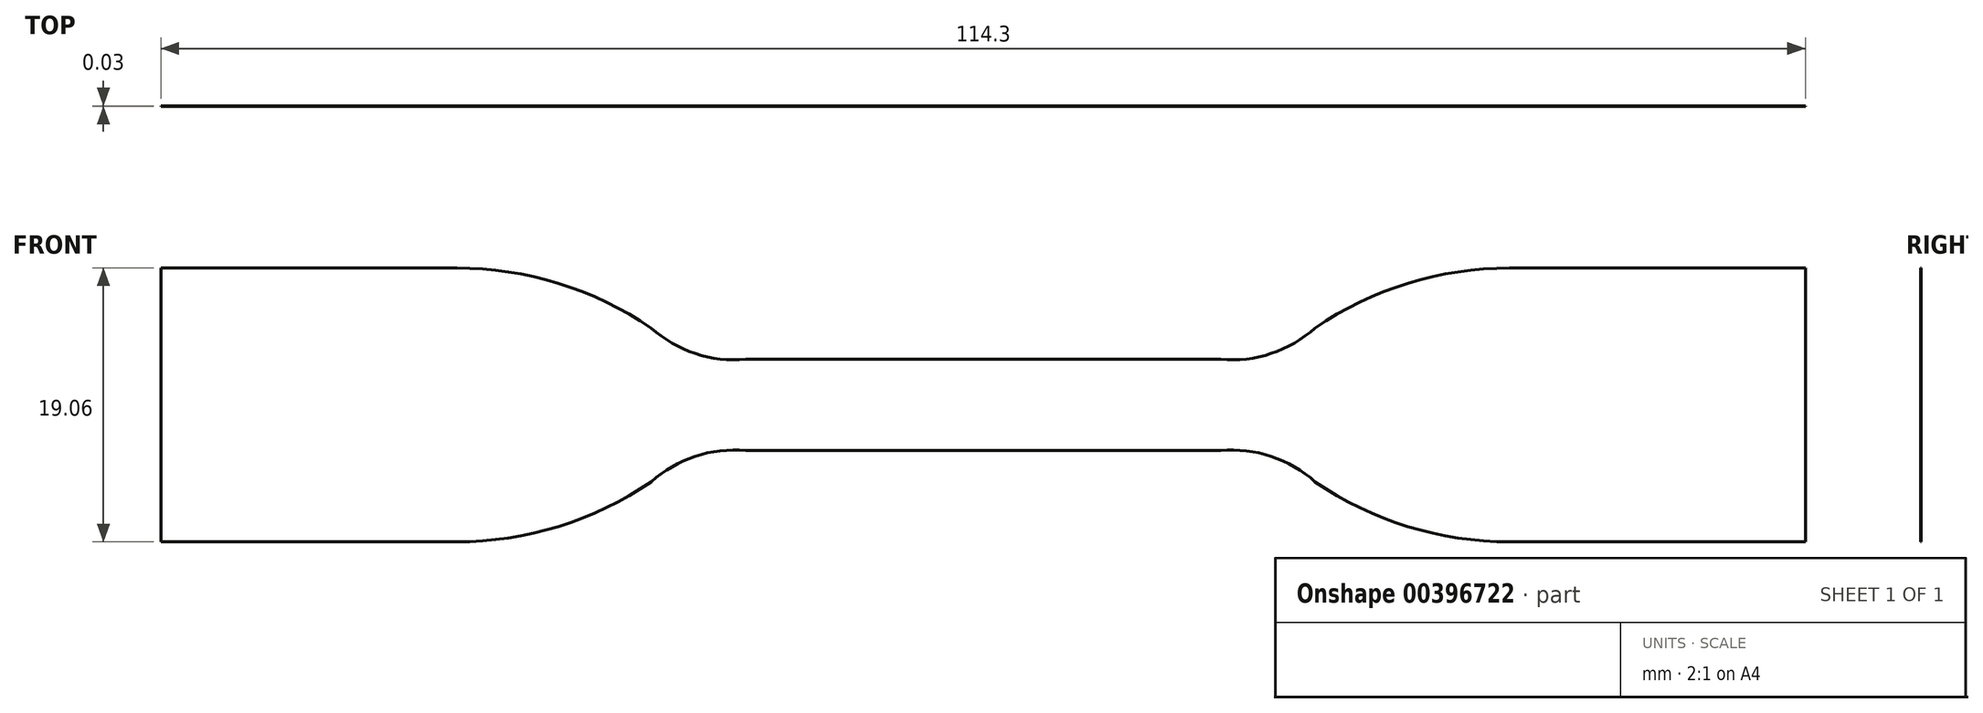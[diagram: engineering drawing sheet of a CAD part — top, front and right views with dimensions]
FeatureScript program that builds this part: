
annotation { "Feature Type Name" : "Feature", "Feature Type Description" : "" }
export const myFeature = defineFeature(function(context is Context, id is Id, definition is map)
    precondition{}
    {
        {
            var Q0;
            Q0=qCreatedBy(makeId("Front.planeOp"),FACE);
            var sketch = newSketch(context, id + "F0", { "sketchPlane" : qUnion([Q0])});
            skLineSegment(sketch, "E0", {"start": v(-57.15, 0) * mm, "end": v(-57.15, -9.52) * mm});
            skLineSegment(sketch, "E1", {"start": v(-57.15, -9.53) * mm, "end": v(-36.58, -9.53) * mm});
            skArc(sketch, "E2", {"start": v(-36.58, -9.53) * mm, "mid": v(-29.51, -8.46) * mm, "end": v(-23.07, -5.35) * mm});
            skArc(sketch, "E3", {"start": v(-16.51, -3.17) * mm, "mid": v(-20.02, -3.58) * mm, "end": v(-23.07, -5.35) * mm});
            skLineSegment(sketch, "E4", {"start": v(-16.51, -3.17) * mm, "end": v(0, -3.17) * mm});
            skArc(sketch, "E5.MirrorCS", {"start": v(-16.51, 3.17) * mm, "mid": v(-20.02, 3.58) * mm, "end": v(-23.07, 5.35) * mm});
            skLineSegment(sketch, "E6.MirrorCS", {"start": v(-16.51, 3.17) * mm, "end": v(0, 3.17) * mm});
            skArc(sketch, "E7.MirrorCS", {"start": v(-36.58, 9.53) * mm, "mid": v(-29.51, 8.46) * mm, "end": v(-23.07, 5.35) * mm});
            skLineSegment(sketch, "E8.MirrorCS", {"start": v(-57.15, 0) * mm, "end": v(-57.15, 9.52) * mm});
            skLineSegment(sketch, "E9.MirrorCS", {"start": v(-57.15, 9.53) * mm, "end": v(-36.58, 9.53) * mm});
            skArc(sketch, "E10.MirrorCS", {"start": v(36.58, -9.53) * mm, "mid": v(29.51, -8.46) * mm, "end": v(23.07, -5.35) * mm});
            skLineSegment(sketch, "E11.MirrorCS", {"start": v(57.15, 0) * mm, "end": v(57.15, -9.52) * mm});
            skArc(sketch, "E12.MirrorCS", {"start": v(16.51, -3.17) * mm, "mid": v(20.02, -3.58) * mm, "end": v(23.07, -5.35) * mm});
            skLineSegment(sketch, "E13.MirrorCS", {"start": v(16.51, 3.17) * mm, "end": v(0, 3.17) * mm});
            skLineSegment(sketch, "E14.MirrorCS", {"start": v(57.15, -9.53) * mm, "end": v(36.58, -9.53) * mm});
            skArc(sketch, "E15.MirrorCS", {"start": v(16.51, 3.17) * mm, "mid": v(20.02, 3.58) * mm, "end": v(23.07, 5.35) * mm});
            skArc(sketch, "E16.MirrorCS", {"start": v(36.58, 9.53) * mm, "mid": v(29.51, 8.46) * mm, "end": v(23.07, 5.35) * mm});
            skLineSegment(sketch, "E17.MirrorCS", {"start": v(57.15, 9.53) * mm, "end": v(36.58, 9.53) * mm});
            skLineSegment(sketch, "E18.MirrorCS", {"start": v(57.15, 0) * mm, "end": v(57.15, 9.52) * mm});
            skLineSegment(sketch, "E19.MirrorCS", {"start": v(16.51, -3.17) * mm, "end": v(0, -3.17) * mm});
            skSolve(sketch);
        }
        {
            var Q0;
            Q0 = qSketchRegion(id + "F0", true);
            extrude(context, id + "F1", {"entities" : qUnion([Q0]), "depth" : 0.03 * mm});
        }
    });
